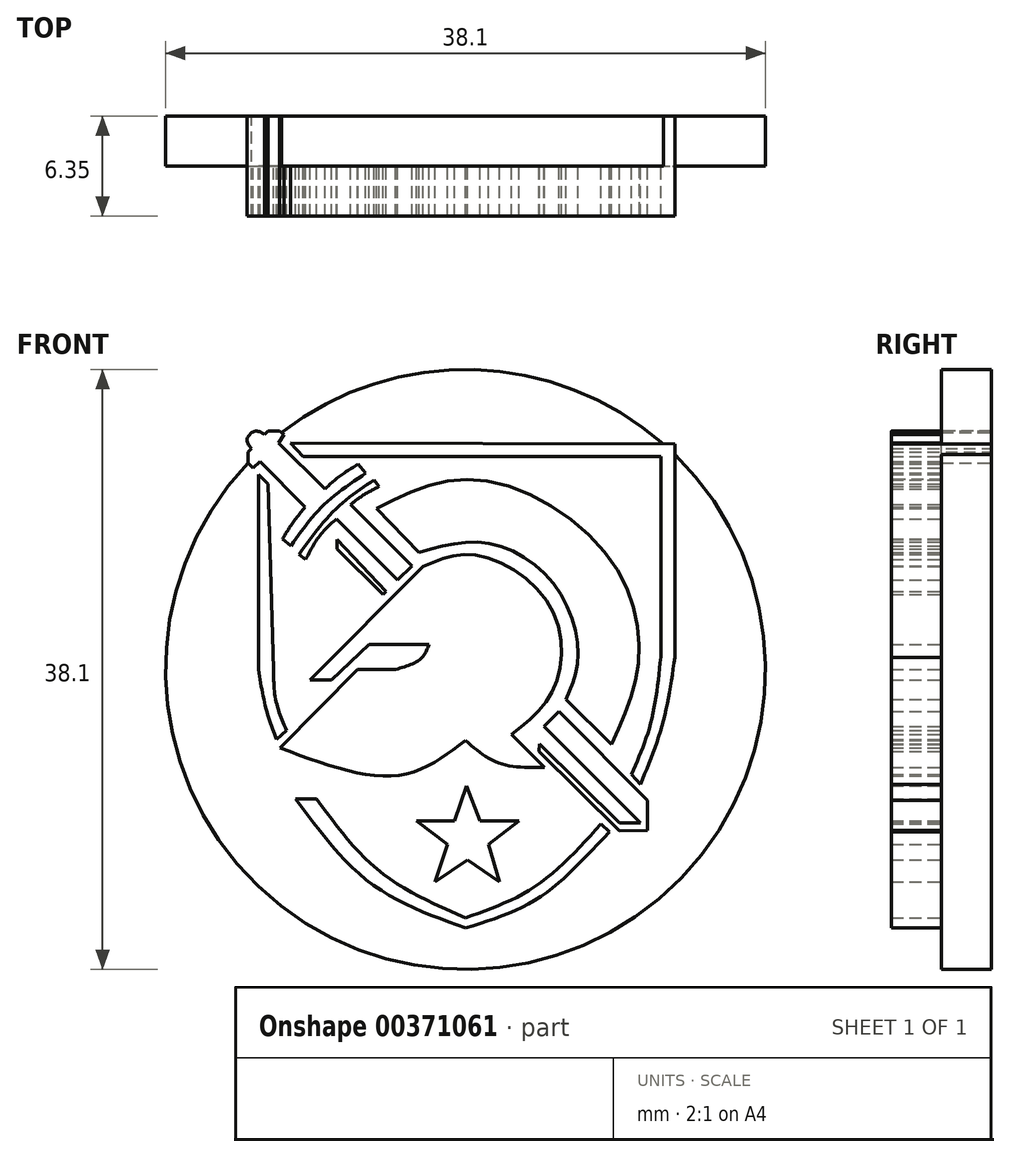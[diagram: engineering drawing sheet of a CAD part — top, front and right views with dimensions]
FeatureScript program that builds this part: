
annotation { "Feature Type Name" : "Feature", "Feature Type Description" : "" }
export const myFeature = defineFeature(function(context is Context, id is Id, definition is map)
    precondition{}
    {
        {
            var Q0;
            Q0=qCreatedBy(makeId("Front.planeOp"),FACE);
            var sketch = newSketch(context, id + "F0", { "sketchPlane" : qUnion([Q0])});
            skCircle(sketch, "E0", {"center": v(0, 0) * mm, "radius": 19.05 * mm});
            skSolve(sketch);
        }
        {
            var Q0;
            Q0 = qSketchRegion(id + "F0", true);
            extrude(context, id + "F1", {"entities" : qUnion([Q0]), "depth" : 3.17 * mm});
        }
        {
            var Q0;
            Q0=makeQuery(id+"F1.opExtrude","CAP_FACE",FACE,{"disambiguationData":[OSD([sQuery(id+"F0.wireOp",EDGE,"E0")])],"isStart":false});
            var sketch = newSketch(context, id + "F2", { "sketchPlane" : qUnion([Q0])});
            skLineSegment(sketch, "E1", {"start": v(-11.12, 14.37) * mm, "end": v(-10.3, 13.53) * mm});
            skLineSegment(sketch, "E2", {"start": v(-10.3, 13.53) * mm, "end": v(12.4, 13.53) * mm});
            skLineSegment(sketch, "E3", {"start": v(12.4, 13.53) * mm, "end": v(12.4, 0.8) * mm});
            skFitSpline(sketch, "E4", {"points": [v(12.4, 0.8) * mm, v(11.74, -3.48) * mm, v(10.54, -6.66) * mm], "startDerivative": vector(-0.9, -8.41) * mm, "endDerivative": vector(-2.87, -6.45) * mm});
            skLineSegment(sketch, "E5", {"start": v(10.54, -6.66) * mm, "end": v(11.1, -7.3) * mm});
            skFitSpline(sketch, "E6", {"points": [v(11.1, -7.3) * mm, v(12.5, -3.48) * mm, v(13.3, 0.78) * mm], "startDerivative": vector(3.18, 7.6) * mm, "endDerivative": vector(1.22, 8.55) * mm});
            skLineSegment(sketch, "E7", {"start": v(13.3, 0.78) * mm, "end": v(13.3, 14.32) * mm});
            skLineSegment(sketch, "E8", {"start": v(13.3, 14.32) * mm, "end": v(-11.12, 14.37) * mm});
            skLineSegment(sketch, "E9", {"start": v(-3.13, -9.62) * mm, "end": v(-0.69, -9.62) * mm});
            skLineSegment(sketch, "E10", {"start": v(-0.69, -9.62) * mm, "end": v(0.06, -7.39) * mm});
            skLineSegment(sketch, "E11", {"start": v(0.06, -7.39) * mm, "end": v(0.92, -9.62) * mm});
            skLineSegment(sketch, "E12", {"start": v(0.92, -9.62) * mm, "end": v(3.4, -9.62) * mm});
            skLineSegment(sketch, "E13", {"start": v(3.4, -9.62) * mm, "end": v(1.47, -11.1) * mm});
            skLineSegment(sketch, "E14", {"start": v(1.47, -11.1) * mm, "end": v(2.17, -13.5) * mm});
            skLineSegment(sketch, "E15", {"start": v(2.17, -13.5) * mm, "end": v(0.13, -12.08) * mm});
            skLineSegment(sketch, "E16", {"start": v(0.13, -12.08) * mm, "end": v(-1.93, -13.5) * mm});
            skLineSegment(sketch, "E17", {"start": v(-1.93, -13.5) * mm, "end": v(-1.15, -11.1) * mm});
            skLineSegment(sketch, "E18", {"start": v(-1.15, -11.1) * mm, "end": v(-3.13, -9.62) * mm});
            skLineSegment(sketch, "E19", {"start": v(11.57, -10.21) * mm, "end": v(11.57, -8.32) * mm});
            skLineSegment(sketch, "E20", {"start": v(11.57, -8.32) * mm, "end": v(5.93, -2.67) * mm});
            skLineSegment(sketch, "E21", {"start": v(5.93, -2.67) * mm, "end": v(4.98, -3.61) * mm});
            skLineSegment(sketch, "E22", {"start": v(4.98, -3.61) * mm, "end": v(11.11, -9.76) * mm});
            skLineSegment(sketch, "E23", {"start": v(11.11, -9.76) * mm, "end": v(9.79, -9.76) * mm});
            skLineSegment(sketch, "E24", {"start": v(9.79, -9.76) * mm, "end": v(4.7, -4.74) * mm});
            skLineSegment(sketch, "E25", {"start": v(4.7, -4.74) * mm, "end": v(4.67, -5.2) * mm});
            skLineSegment(sketch, "E26", {"start": v(2.92, -4.14) * mm, "end": v(5.02, -6.2) * mm});
            skLineSegment(sketch, "E27", {"start": v(5.74, -6.9) * mm, "end": v(6.13, -7.28) * mm});
            skLineSegment(sketch, "E28", {"start": v(8.6, -9.82) * mm, "end": v(9.14, -10.32) * mm});
            skLineSegment(sketch, "E29", {"start": v(9.25, -4.77) * mm, "end": v(6.38, -1.9) * mm});
            skFitSpline(sketch, "E30", {"points": [v(-5.65, 10.21) * mm, v(0.84, 12.05) * mm, v(9.06, 7.18) * mm, v(10.98, 0.45) * mm, v(9.25, -4.77) * mm], "startDerivative": vector(25.1, 12.78) * mm, "endDerivative": vector(-10.44, -22.69) * mm});
            skLineSegment(sketch, "E31", {"start": v(-5.65, 10.21) * mm, "end": v(-2.94, 7.45) * mm});
            skFitSpline(sketch, "E32", {"points": [v(-2.94, 7.45) * mm, v(1.41, 8.02) * mm, v(5.68, 5.33) * mm, v(7.14, 0.78) * mm, v(6.38, -1.9) * mm], "startDerivative": vector(16.86, 4.75) * mm, "endDerivative": vector(-5.31, -11.96) * mm});
            skLineSegment(sketch, "E33", {"start": v(-4.18, 9.45) * mm, "end": v(-2.86, 8.1) * mm});
            skLineSegment(sketch, "E34", {"start": v(-2.92, 9.93) * mm, "end": v(-2.27, 8.24) * mm});
            skLineSegment(sketch, "E35", {"start": v(-2.3, 10.01) * mm, "end": v(-1.74, 8.41) * mm});
            skLineSegment(sketch, "E36", {"start": v(-1.15, 10.2) * mm, "end": v(-0.87, 8.53) * mm});
            skLineSegment(sketch, "E37", {"start": v(-0.42, 10.4) * mm, "end": v(-0.42, 8.64) * mm});
            skLineSegment(sketch, "E38", {"start": v(0.73, 10.3) * mm, "end": v(0.73, 8.64) * mm});
            skLineSegment(sketch, "E39", {"start": v(-7.3, 10.5) * mm, "end": v(-3.4, 6.59) * mm});
            skLineSegment(sketch, "E40", {"start": v(-3.4, 6.59) * mm, "end": v(-4.3, 5.68) * mm});
            skLineSegment(sketch, "E41", {"start": v(-4.3, 5.68) * mm, "end": v(-8.2, 9.56) * mm});
            skFitSpline(sketch, "E42", {"points": [v(-8.2, 9.56) * mm, v(-9.26, 8.5) * mm, v(-10.16, 6.98) * mm], "startDerivative": vector(-2.34, -2.05) * mm, "endDerivative": vector(-1.6, -3.1) * mm});
            skFitSpline(sketch, "E43", {"points": [v(-7.3, 10.5) * mm, v(-6.48, 11.08) * mm, v(-5.5, 11.61) * mm], "startDerivative": vector(1.61, 1.25) * mm, "endDerivative": vector(1.98, 1) * mm});
            skLineSegment(sketch, "E44", {"start": v(-10.16, 6.98) * mm, "end": v(-10.58, 7.32) * mm});
            skLineSegment(sketch, "E45", {"start": v(-5.5, 11.61) * mm, "end": v(-5.8, 12.03) * mm});
            skFitSpline(sketch, "E46", {"points": [v(-5.8, 12.03) * mm, v(-8.2, 10.24) * mm, v(-10.58, 7.32) * mm], "startDerivative": vector(-5.2, -3.41) * mm, "endDerivative": vector(-4.36, -5.97) * mm});
            skLineSegment(sketch, "E47", {"start": v(-8.16, 8.24) * mm, "end": v(-8.16, 7.66) * mm});
            skLineSegment(sketch, "E48", {"start": v(-8.16, 7.66) * mm, "end": v(-5.24, 4.76) * mm});
            skLineSegment(sketch, "E49", {"start": v(-5.24, 4.76) * mm, "end": v(-5.05, 4.96) * mm});
            skLineSegment(sketch, "E50", {"start": v(-5.05, 4.96) * mm, "end": v(-8.16, 8.24) * mm});
            skLineSegment(sketch, "E51", {"start": v(-2.7, 6.53) * mm, "end": v(-9.89, -0.67) * mm});
            skLineSegment(sketch, "E52", {"start": v(-9.89, -0.67) * mm, "end": v(-8.51, -0.67) * mm});
            skLineSegment(sketch, "E53", {"start": v(-8.51, -0.67) * mm, "end": v(-6.13, 1.59) * mm});
            skLineSegment(sketch, "E54", {"start": v(-6.13, 1.59) * mm, "end": v(-2.3, 1.59) * mm});
            skFitSpline(sketch, "E55", {"points": [v(-2.3, 1.59) * mm, v(-2.86, 0.66) * mm, v(-4.45, 0) * mm], "startDerivative": vector(-0.9, -2.3) * mm, "endDerivative": vector(-3.28, -0.94) * mm});
            skLineSegment(sketch, "E56", {"start": v(-4.45, 0) * mm, "end": v(-6.86, 0) * mm});
            skLineSegment(sketch, "E57", {"start": v(-6.86, 0) * mm, "end": v(-11.78, -4.97) * mm});
            skFitSpline(sketch, "E58", {"points": [v(-11.78, -4.97) * mm, v(-4.32, -6.73) * mm, v(0, -4.5) * mm], "startDerivative": vector(14.43, -5.44) * mm, "endDerivative": vector(8.93, 6.84) * mm});
            skFitSpline(sketch, "E59", {"points": [v(0, -4.5) * mm, v(2.14, -5.95) * mm, v(5.02, -6.2) * mm], "startDerivative": vector(4.1, -3.58) * mm, "endDerivative": vector(5.9, 0.14) * mm});
            skFitSpline(sketch, "E60", {"points": [v(2.92, -4.14) * mm, v(5.65, -1.1) * mm, v(5.34, 4.06) * mm, v(0.61, 7.26) * mm, v(-2.7, 6.53) * mm], "startDerivative": vector(13.66, 10.9) * mm, "endDerivative": vector(-14.14, -6.26) * mm});
            skLineSegment(sketch, "E61", {"start": v(-10.2, 10.31) * mm, "end": v(-13.06, 13.22) * mm});
            skLineSegment(sketch, "E62", {"start": v(-13.06, 13.22) * mm, "end": v(-13.48, 12.8) * mm});
            skLineSegment(sketch, "E63", {"start": v(-13.48, 12.8) * mm, "end": v(-13.81, 13.11) * mm});
            skLineSegment(sketch, "E64", {"start": v(-13.81, 13.11) * mm, "end": v(-13.81, 13.82) * mm});
            skLineSegment(sketch, "E65", {"start": v(-13.81, 13.82) * mm, "end": v(-13.59, 14.03) * mm});
            skFitSpline(sketch, "E66", {"points": [v(-13.59, 14.02) * mm, v(-13.87, 14.64) * mm, v(-13.37, 15.14) * mm, v(-12.77, 14.94) * mm], "startDerivative": vector(-1.42, 1.8) * mm, "endDerivative": vector(1.8, -1.13) * mm});
            skLineSegment(sketch, "E67", {"start": v(-12.77, 14.94) * mm, "end": v(-12.53, 15.14) * mm});
            skLineSegment(sketch, "E68", {"start": v(-12.53, 15.14) * mm, "end": v(-11.81, 15.14) * mm});
            skLineSegment(sketch, "E69", {"start": v(-11.81, 15.14) * mm, "end": v(-11.51, 14.94) * mm});
            skLineSegment(sketch, "E70", {"start": v(-11.51, 14.94) * mm, "end": v(-11.88, 14.39) * mm});
            skLineSegment(sketch, "E71", {"start": v(-11.88, 14.39) * mm, "end": v(-8.93, 11.46) * mm});
            skFitSpline(sketch, "E72", {"points": [v(-8.93, 11.46) * mm, v(-8.1, 12.2) * mm, v(-6.83, 13.04) * mm], "startDerivative": vector(1.7, 1.6) * mm, "endDerivative": vector(2.48, 1.55) * mm});
            skFitSpline(sketch, "E73", {"points": [v(-10.2, 10.31) * mm, v(-11.01, 9.26) * mm, v(-11.63, 8.28) * mm], "startDerivative": vector(-1.65, -2.04) * mm, "endDerivative": vector(-1.21, -2.03) * mm});
            skFitSpline(sketch, "E74", {"points": [v(-11.07, 7.86) * mm, v(-9.15, 10.31) * mm, v(-6.33, 12.48) * mm], "startDerivative": vector(3.6, 5.28) * mm, "endDerivative": vector(5.84, 3.97) * mm});
            skLineSegment(sketch, "E75", {"start": v(-11.63, 8.28) * mm, "end": v(-11.07, 7.86) * mm});
            skLineSegment(sketch, "E76", {"start": v(-6.83, 13.04) * mm, "end": v(-6.33, 12.48) * mm});
            skLineSegment(sketch, "E77", {"start": v(-13.16, 11.77) * mm, "end": v(-13.16, 0) * mm});
            skPoint(sketch, "E77.startSnap0", {"position": v(-11.63, 11.77) * mm});
            skLineSegment(sketch, "E78", {"start": v(-13.16, 11.77) * mm, "end": v(-13.16, 12.4) * mm});
            skLineSegment(sketch, "E79", {"start": v(-13.16, 12.4) * mm, "end": v(-12.53, 11.77) * mm});
            skFitSpline(sketch, "E80", {"points": [v(-12, -4.45) * mm, v(-12.66, -2.53) * mm, v(-13.16, 0) * mm], "startDerivative": vector(-1.53, 3.92) * mm, "endDerivative": vector(-0.8, 4.95) * mm});
            skFitSpline(sketch, "E81", {"points": [v(-11.38, -3.86) * mm, v(-12.04, -1.96) * mm, v(-12.2, 0) * mm], "startDerivative": vector(-1.58, 3.74) * mm, "endDerivative": vector(-0.06, 3.99) * mm});
            skLineSegment(sketch, "E82", {"start": v(-12.2, 0) * mm, "end": v(-12.53, 11.77) * mm});
            skLineSegment(sketch, "E83", {"start": v(-11.38, -3.86) * mm, "end": v(-12, -4.45) * mm});
            skFitSpline(sketch, "E84", {"points": [v(-9.46, -8.22) * mm, v(-5.42, -12.84) * mm, v(0, -15.77) * mm], "startDerivative": vector(7.4, -10.1) * mm, "endDerivative": vector(11.52, -5.01) * mm});
            skFitSpline(sketch, "E85", {"points": [v(-10.78, -8.22) * mm, v(-5.94, -13.64) * mm, v(0, -16.42) * mm], "startDerivative": vector(8.73, -11.7) * mm, "endDerivative": vector(12.3, -4.61) * mm});
            skFitSpline(sketch, "E86", {"points": [v(8.6, -9.82) * mm, v(4.4, -13.79) * mm, v(0, -15.77) * mm], "startDerivative": vector(-7.73, -8.5) * mm, "endDerivative": vector(-9.5, -3.32) * mm});
            skFitSpline(sketch, "E87", {"points": [v(9.14, -10.32) * mm, v(4.85, -14.38) * mm, v(0, -16.42) * mm], "startDerivative": vector(-8.91, -9.04) * mm, "endDerivative": vector(-10.96, -3.3) * mm});
            skLineSegment(sketch, "E88", {"start": v(-9.46, -8.22) * mm, "end": v(-10.78, -8.22) * mm});
            skLineSegment(sketch, "E89", {"start": v(4.67, -5.2) * mm, "end": v(9.78, -10.26) * mm});
            skLineSegment(sketch, "E90", {"start": v(9.78, -10.26) * mm, "end": v(11.57, -10.21) * mm});
            skSolve(sketch);
        }
        {
            var Q0;
            Q0 = qSketchRegion(id + "F2", true);
            var Q1;
            Q1=makeQuery(id+"F1.opExtrude","CAP_FACE",FACE,{"disambiguationData":[OSD([sQuery(id+"F0.wireOp",EDGE,"E0")])],"isStart":true});
            extrude(context, id + "F3", {"entities" : qUnion([Q0]), "operationType" : NewBodyOperationType.ADD, "offsetDistance" : 25.4 * mm, "depth" : 3.17 * mm, "hasSecondDirection" : true, "secondDirectionBound" : SecondDirectionBoundingType.UP_TO_SURFACE, "secondDirectionOppositeDirection" : true, "secondDirectionBoundEntityFace" : qUnion([Q1]), "secondDirectionDepth" : 25.4 * mm});
        }
    });
